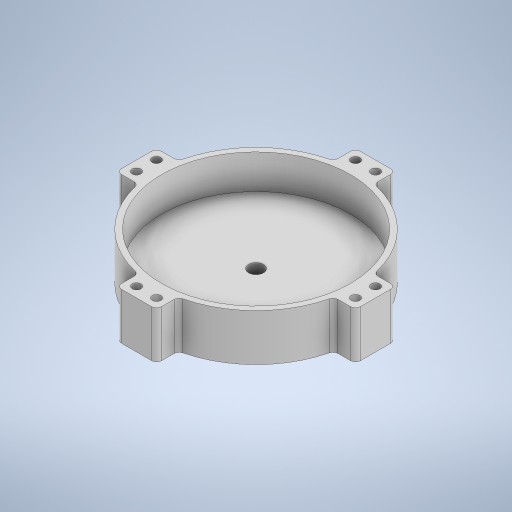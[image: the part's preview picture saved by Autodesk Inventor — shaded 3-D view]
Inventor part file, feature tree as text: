
AUTODESK INVENTOR PART (.ipt)
format: ipt  version: 2023 (Build 270158000, 158)  size: 709,632 bytes
history: native  units: in
note: dims shown in document units (in); Inventor stores cm internally (conversion verified against a paired STEP export)
features: extrude x3, sketch x3, fillet x2
ambient origin geometry x8: Origin, YZ Plane, XZ Plane, XY Plane, X Axis, Y Axis, Z Axis, Center Point
bodies: Solid1 (feature_tree)
feature tree (8):
  extrude  "Extrusion1"  Depth=0.3in
  extrude  "Extrusion2"  Depth=0.687in
  fillet  "Fillet1"  Radius=0.687in
  extrude  "Extrusion3"  Depth=0.1in
  fillet  "Fillet2"  Radius=0.5in
  sketch  "Sketch1"  dims[d0=4.0in d1=0.3in]
  sketch  "Sketch2"  dims[d2=0.25in d3=0.0in d4=3.78in d5=0.687in d6=0.0in]
  sketch  "Sketch3"  dims[d7=0.05in d8=0.4in d9=0.5in d10=0.5in d11=0.4in d12=0.4in d13=0.4in d14=0.5in d15=0.4in d16=0.4in d17=0.5in d18=0.4in d19=0.4in d20=0.2in d21=0.2in d22=0.2in d23=0.177in d24=0.177in d25=0.177in d26=0.177in d27=0.177in d28=0.177in d29=0.177in d30=0.177in d31=1.0in d32=0.0in d33=0.1in]
